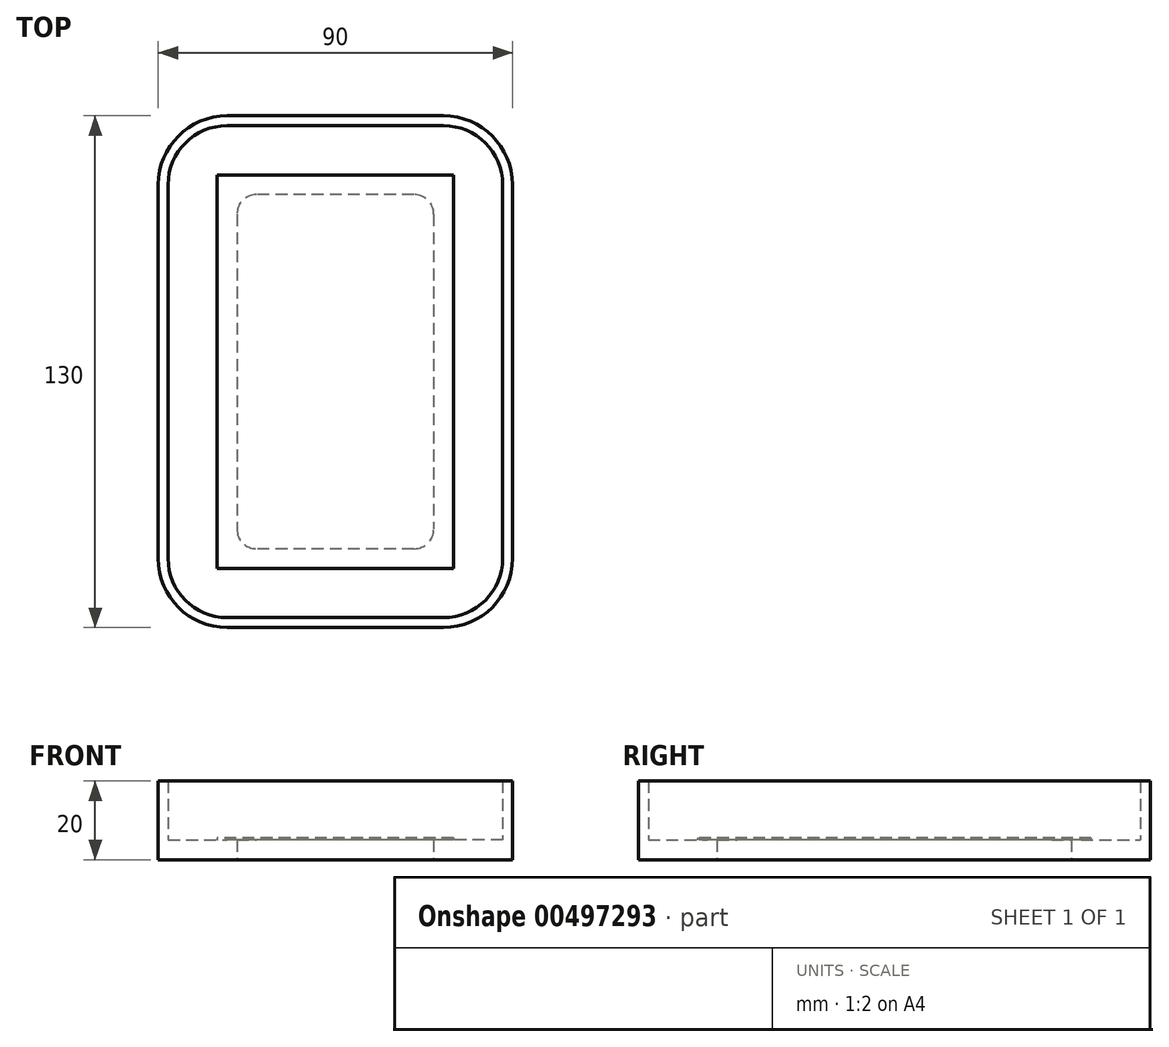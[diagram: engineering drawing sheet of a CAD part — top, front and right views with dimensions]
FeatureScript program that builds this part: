
annotation { "Feature Type Name" : "Feature", "Feature Type Description" : "" }
export const myFeature = defineFeature(function(context is Context, id is Id, definition is map)
    precondition{}
    {
        {
            var Q0;
            Q0=qCreatedBy(makeId("Top.planeOp"),FACE);
            var sketch = newSketch(context, id + "F0", { "sketchPlane" : qUnion([Q0])});
            skLineSegment(sketch, "E0.bottom", {"start": v(27.5, 62.5) * mm, "end": v(-27.5, 62.5) * mm});
            skLineSegment(sketch, "E0.top", {"start": v(27.5, -62.5) * mm, "end": v(-27.5, -62.5) * mm});
            skLineSegment(sketch, "E0.left", {"start": v(42.5, 47.5) * mm, "end": v(42.5, -47.5) * mm});
            skLineSegment(sketch, "E0.right", {"start": v(-42.5, 47.5) * mm, "end": v(-42.5, -47.5) * mm});
            skPoint(sketch, "E0.middle", {"position": v(0, 0) * mm});
            skLineSegment(sketch, "E1.0", {"start": v(20, 47.5) * mm, "end": v(-20, 47.5) * mm});
            skLineSegment(sketch, "E1.1", {"start": v(27.5, 40) * mm, "end": v(27.5, -40) * mm});
            skLineSegment(sketch, "E1.2", {"start": v(20, -47.5) * mm, "end": v(-20, -47.5) * mm});
            skLineSegment(sketch, "E1.3", {"start": v(-27.5, 40) * mm, "end": v(-27.5, -40) * mm});
            skPoint(sketch, "E2.visualSharp", {"position": v(-27.5, 47.5) * mm});
            skArc(sketch, "E2.filletArc", {"start": v(-20, 47.5) * mm, "mid": v(-25.3, 45.3) * mm, "end": v(-27.5, 40) * mm});
            skPoint(sketch, "E3.visualSharp", {"position": v(27.5, 47.5) * mm});
            skArc(sketch, "E3.filletArc", {"start": v(27.5, 40) * mm, "mid": v(25.3, 45.3) * mm, "end": v(20, 47.5) * mm});
            skPoint(sketch, "E4.visualSharp", {"position": v(27.5, -47.5) * mm});
            skArc(sketch, "E4.filletArc", {"start": v(20, -47.5) * mm, "mid": v(25.3, -45.3) * mm, "end": v(27.5, -40) * mm});
            skPoint(sketch, "E5.visualSharp", {"position": v(-27.5, -47.5) * mm});
            skArc(sketch, "E5.filletArc", {"start": v(-27.5, -40) * mm, "mid": v(-25.3, -45.3) * mm, "end": v(-20, -47.5) * mm});
            skArc(sketch, "E6.0", {"start": v(25, 40) * mm, "mid": v(23.54, 43.54) * mm, "end": v(20, 45) * mm});
            skLineSegment(sketch, "E6.1", {"start": v(20, 45) * mm, "end": v(-20, 45) * mm});
            skLineSegment(sketch, "E6.2", {"start": v(25, 40) * mm, "end": v(25, -40) * mm});
            skArc(sketch, "E6.3", {"start": v(-20, 45) * mm, "mid": v(-23.54, 43.54) * mm, "end": v(-25, 40) * mm});
            skArc(sketch, "E6.4", {"start": v(20, -45) * mm, "mid": v(23.54, -43.54) * mm, "end": v(25, -40) * mm});
            skLineSegment(sketch, "E6.5", {"start": v(20, -45) * mm, "end": v(-20, -45) * mm});
            skArc(sketch, "E6.6", {"start": v(-25, -40) * mm, "mid": v(-23.54, -43.54) * mm, "end": v(-20, -45) * mm});
            skLineSegment(sketch, "E6.7", {"start": v(-25, 40) * mm, "end": v(-25, -40) * mm});
            skPoint(sketch, "E7.visualSharp", {"position": v(-42.5, 62.5) * mm});
            skArc(sketch, "E7.filletArc", {"start": v(-27.5, 62.5) * mm, "mid": v(-38.1, 58.1) * mm, "end": v(-42.5, 47.5) * mm});
            skPoint(sketch, "E8.visualSharp", {"position": v(42.5, 62.5) * mm});
            skArc(sketch, "E8.filletArc", {"start": v(42.5, 47.5) * mm, "mid": v(38.1, 58.1) * mm, "end": v(27.5, 62.5) * mm});
            skPoint(sketch, "E9.visualSharp", {"position": v(42.5, -62.5) * mm});
            skArc(sketch, "E9.filletArc", {"start": v(27.5, -62.5) * mm, "mid": v(38.1, -58.1) * mm, "end": v(42.5, -47.5) * mm});
            skPoint(sketch, "E10.visualSharp", {"position": v(-42.5, -62.5) * mm});
            skArc(sketch, "E10.filletArc", {"start": v(-42.5, -47.5) * mm, "mid": v(-38.1, -58.1) * mm, "end": v(-27.5, -62.5) * mm});
            skArc(sketch, "E11.0", {"start": v(45, 47.5) * mm, "mid": v(39.87, 59.87) * mm, "end": v(27.5, 65) * mm});
            skLineSegment(sketch, "E11.1", {"start": v(27.5, 65) * mm, "end": v(-27.5, 65) * mm});
            skLineSegment(sketch, "E11.2", {"start": v(45, 47.5) * mm, "end": v(45, -47.5) * mm});
            skArc(sketch, "E11.3", {"start": v(-27.5, 65) * mm, "mid": v(-39.87, 59.87) * mm, "end": v(-45, 47.5) * mm});
            skArc(sketch, "E11.4", {"start": v(27.5, -65) * mm, "mid": v(39.87, -59.87) * mm, "end": v(45, -47.5) * mm});
            skLineSegment(sketch, "E11.5", {"start": v(27.5, -65) * mm, "end": v(-27.5, -65) * mm});
            skArc(sketch, "E11.6", {"start": v(-45, -47.5) * mm, "mid": v(-39.87, -59.87) * mm, "end": v(-27.5, -65) * mm});
            skLineSegment(sketch, "E11.7", {"start": v(-45, 47.5) * mm, "end": v(-45, -47.5) * mm});
            skSolve(sketch);
        }
        {
            var Q0;
            Q0=makeQuery(id+"F0.imprint","IMPRINT",FACE,{"disambiguationData":[TD([[makeQuery(id+"F0.imprint","IMPRINT",EDGE,{"derivedFrom":sQuery(id+"F0.wireOp",EDGE,"E0.bottom")}),-1.0]])]});
            extrude(context, id + "F1", {"entities" : qUnion([Q0]), "depth" : 20 * mm});
        }
        {
            var Q0;
            Q0=makeQuery(id+"F0.imprint","IMPRINT",FACE,{"disambiguationData":[TD([[makeQuery(id+"F0.imprint","IMPRINT",EDGE,{"derivedFrom":sQuery(id+"F0.wireOp",EDGE,"E0.bottom")}),1.0]])]});
            var Q1;
            Q1=makeQuery(id+"F0.imprint","IMPRINT",FACE,{"disambiguationData":[TD([[makeQuery(id+"F0.imprint","IMPRINT",EDGE,{"derivedFrom":sQuery(id+"F0.wireOp",EDGE,"E1.0")}),1.0]])]});
            extrude(context, id + "F2", {"entities" : qUnion([Q0, Q1]), "operationType" : NewBodyOperationType.ADD, "depth" : 5 * mm});
        }
        {
            var Q0;
            Q0=makeQuery(id+"F2.opExtrude","CAP_FACE",FACE,{"disambiguationData":[OSD([sQuery(id+"F0.wireOp",EDGE,"E0.bottom"),sQuery(id+"F0.wireOp",EDGE,"E0.top"),sQuery(id+"F0.wireOp",EDGE,"E0.left"),sQuery(id+"F0.wireOp",EDGE,"E0.right"),sQuery(id+"F0.wireOp",EDGE,"E6.0"),sQuery(id+"F0.wireOp",EDGE,"E6.1"),sQuery(id+"F0.wireOp",EDGE,"E6.2"),sQuery(id+"F0.wireOp",EDGE,"E6.3"),sQuery(id+"F0.wireOp",EDGE,"E6.4"),sQuery(id+"F0.wireOp",EDGE,"E6.5"),sQuery(id+"F0.wireOp",EDGE,"E6.6"),sQuery(id+"F0.wireOp",EDGE,"E6.7"),sQuery(id+"F0.wireOp",EDGE,"E7.filletArc"),sQuery(id+"F0.wireOp",EDGE,"E8.filletArc"),sQuery(id+"F0.wireOp",EDGE,"E9.filletArc"),sQuery(id+"F0.wireOp",EDGE,"E10.filletArc")])],"isStart":false});
            var sketch = newSketch(context, id + "F3", { "sketchPlane" : qUnion([Q0])});
            skLineSegment(sketch, "E12.0", {"start": v(30, 50) * mm, "end": v(30, -50) * mm});
            skLineSegment(sketch, "E12.1", {"start": v(30, 50) * mm, "end": v(-30, 50) * mm});
            skLineSegment(sketch, "E12.2", {"start": v(-30, 50) * mm, "end": v(-30, -50) * mm});
            skLineSegment(sketch, "E12.3", {"start": v(30, -50) * mm, "end": v(-30, -50) * mm});
            skSolve(sketch);
        }
        {
            var Q0;
            Q0 = qSketchRegion(id + "F3", true);
            extrude(context, id + "F4", {"entities" : qUnion([Q0]), "operationType" : NewBodyOperationType.ADD, "depth" : 0.5 * mm, "offsetDistance" : 25 * mm});
        }
    });
